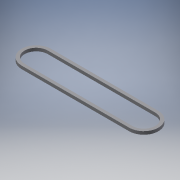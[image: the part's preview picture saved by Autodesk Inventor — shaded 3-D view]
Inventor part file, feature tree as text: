
AUTODESK INVENTOR PART (.ipt)
format: ipt  version: 2017 (Build 210142000, 142)  size: 104,448 bytes
history: native  units: mm
features: other x4, reference x2, extrude x1, sketch x1
ambient origin geometry x8: Origin, YZ Plane, XZ Plane, XY Plane, X Axis, Y Axis, Z Axis, Center Point
bodies: Solid1 (feature_tree)
feature tree (8):
  extrude  "Extrusion1"  Depth=8.0mm TaperAngle=0.0deg
  sketch  "Sketch1"  dims[d0=8.0mm d1=8.0mm d2=0.0mm]
  reference  "Reference1"
  reference  "Reference2"
  other  "<userpath>\OneDrive\Inventor\VolledigGeassembleerdv001.iam"
  other  "VolledigGeassembleerdv001.iam"
  other  "kettingwiel:1"
  other  "kettingwiel:2"
